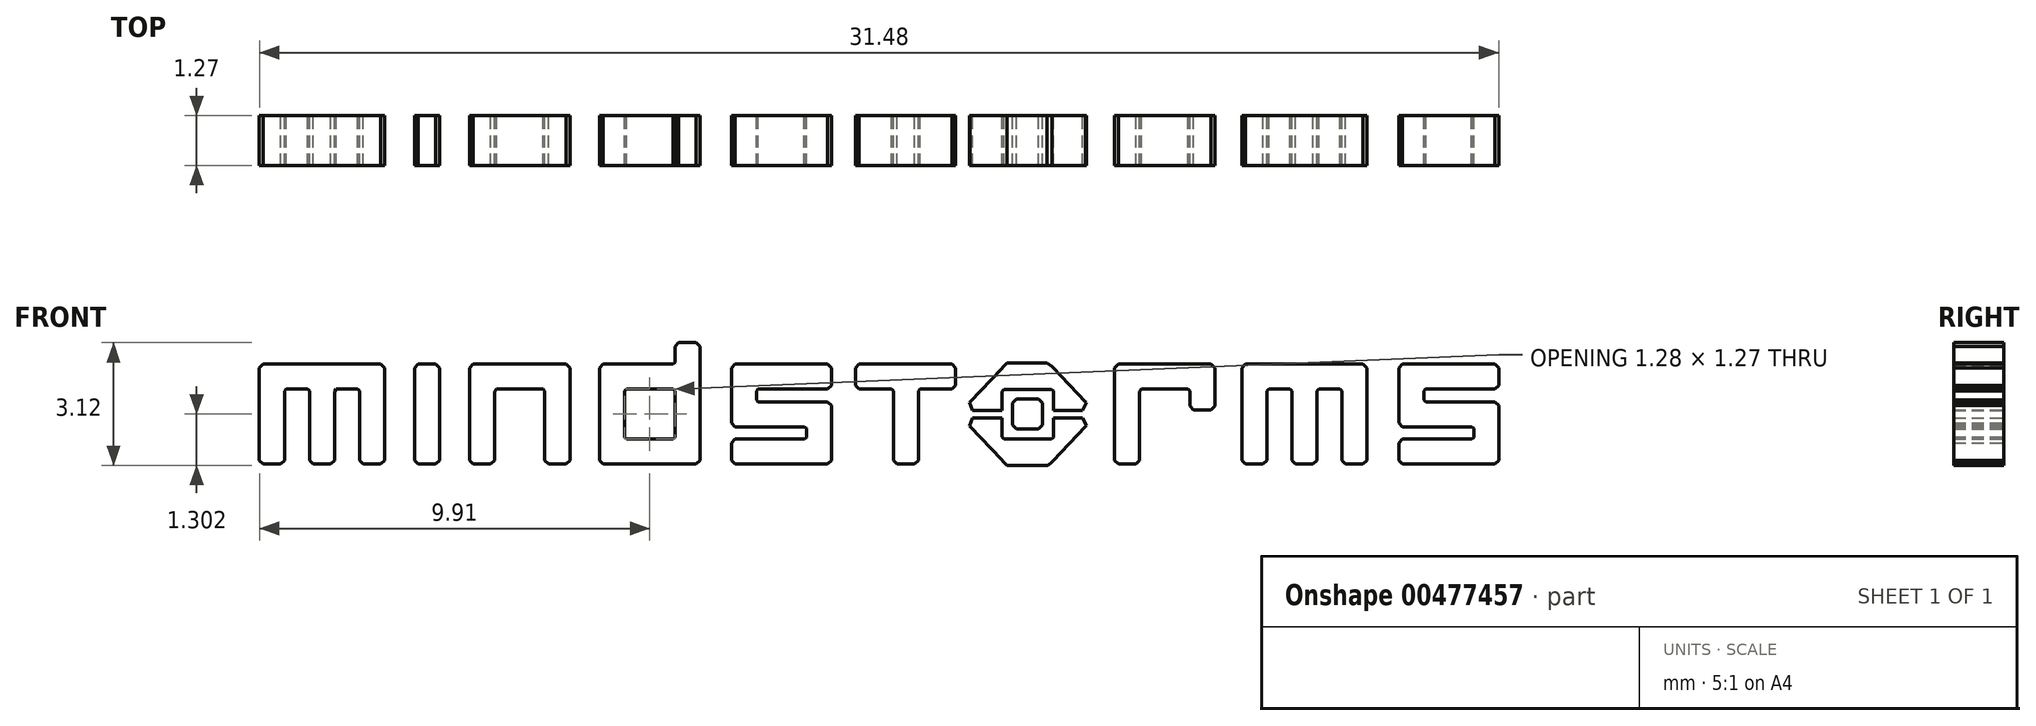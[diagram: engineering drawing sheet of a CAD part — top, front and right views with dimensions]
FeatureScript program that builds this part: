
annotation { "Feature Type Name" : "Feature", "Feature Type Description" : "" }
export const myFeature = defineFeature(function(context is Context, id is Id, definition is map)
    precondition{}
    {
        {
            var Q0;
            Q0=qCreatedBy(makeId("Front.planeOp"),FACE);
            var sketch = newSketch(context, id + "F0", { "sketchPlane" : qUnion([Q0])});
            skLineSegment(sketch, "E0", {"start": v(4.43, -0.35) * mm, "end": v(5.14, -0.35) * mm});
            skLineSegment(sketch, "E1", {"start": v(5.14, -0.35) * mm, "end": v(5.17, -0.35) * mm});
            skLineSegment(sketch, "E2", {"start": v(5.17, -0.35) * mm, "end": v(5.26, -0.55) * mm});
            skLineSegment(sketch, "E3", {"start": v(5.26, -0.55) * mm, "end": v(5.25, -0.57) * mm});
            skLineSegment(sketch, "E4", {"start": v(5.25, -0.57) * mm, "end": v(4.42, -1.44) * mm});
            skLineSegment(sketch, "E5", {"start": v(4.42, -1.44) * mm, "end": v(4.38, -1.47) * mm});
            skLineSegment(sketch, "E6", {"start": v(4.38, -1.47) * mm, "end": v(4.29, -1.56) * mm});
            skLineSegment(sketch, "E7", {"start": v(4.29, -1.56) * mm, "end": v(4.25, -1.56) * mm});
            skLineSegment(sketch, "E8", {"start": v(4.25, -1.56) * mm, "end": v(3.3, -1.56) * mm});
            skLineSegment(sketch, "E9", {"start": v(3.3, -1.56) * mm, "end": v(3.25, -1.56) * mm});
            skLineSegment(sketch, "E10", {"start": v(3.25, -1.56) * mm, "end": v(3.15, -1.46) * mm});
            skLineSegment(sketch, "E11", {"start": v(3.15, -1.46) * mm, "end": v(3.11, -1.42) * mm});
            skLineSegment(sketch, "E12", {"start": v(3.11, -1.42) * mm, "end": v(2.3, -0.57) * mm});
            skLineSegment(sketch, "E13", {"start": v(2.3, -0.57) * mm, "end": v(2.3, -0.55) * mm});
            skLineSegment(sketch, "E14", {"start": v(2.3, -0.55) * mm, "end": v(2.38, -0.35) * mm});
            skLineSegment(sketch, "E15", {"start": v(2.38, -0.35) * mm, "end": v(2.4, -0.35) * mm});
            skLineSegment(sketch, "E16", {"start": v(2.4, -0.35) * mm, "end": v(3.12, -0.35) * mm});
            skLineSegment(sketch, "E17", {"start": v(3.12, -0.35) * mm, "end": v(3.12, -0.83) * mm});
            skLineSegment(sketch, "E18", {"start": v(3.12, -0.83) * mm, "end": v(3.12, -0.84) * mm});
            skLineSegment(sketch, "E19", {"start": v(3.12, -0.84) * mm, "end": v(3.17, -0.9) * mm});
            skLineSegment(sketch, "E20", {"start": v(3.17, -0.9) * mm, "end": v(3.18, -0.9) * mm});
            skLineSegment(sketch, "E21", {"start": v(3.18, -0.9) * mm, "end": v(4.36, -0.9) * mm});
            skLineSegment(sketch, "E22", {"start": v(4.36, -0.9) * mm, "end": v(4.38, -0.9) * mm});
            skLineSegment(sketch, "E23", {"start": v(4.38, -0.9) * mm, "end": v(4.43, -0.84) * mm});
            skLineSegment(sketch, "E24", {"start": v(4.43, -0.84) * mm, "end": v(4.43, -0.83) * mm});
            skLineSegment(sketch, "E25", {"start": v(4.43, -0.83) * mm, "end": v(4.43, -0.35) * mm});
            skLineSegment(sketch, "E26", {"start": v(4.43, -0.16) * mm, "end": v(5.14, -0.16) * mm});
            skLineSegment(sketch, "E27", {"start": v(5.14, -0.16) * mm, "end": v(5.17, -0.16) * mm});
            skLineSegment(sketch, "E28", {"start": v(5.17, -0.16) * mm, "end": v(5.26, 0.04) * mm});
            skLineSegment(sketch, "E29", {"start": v(5.26, 0.04) * mm, "end": v(5.25, 0.05) * mm});
            skLineSegment(sketch, "E30", {"start": v(5.25, 0.05) * mm, "end": v(4.42, 0.93) * mm});
            skLineSegment(sketch, "E31", {"start": v(4.42, 0.93) * mm, "end": v(4.39, 0.96) * mm});
            skLineSegment(sketch, "E32", {"start": v(4.39, 0.96) * mm, "end": v(4.26, 1.05) * mm});
            skLineSegment(sketch, "E33", {"start": v(4.26, 1.05) * mm, "end": v(4.25, 1.05) * mm});
            skLineSegment(sketch, "E34", {"start": v(4.25, 1.05) * mm, "end": v(3.3, 1.05) * mm});
            skLineSegment(sketch, "E35", {"start": v(3.3, 1.05) * mm, "end": v(3.25, 1.05) * mm});
            skLineSegment(sketch, "E36", {"start": v(3.25, 1.05) * mm, "end": v(3.15, 0.94) * mm});
            skLineSegment(sketch, "E37", {"start": v(3.15, 0.94) * mm, "end": v(3.11, 0.9) * mm});
            skLineSegment(sketch, "E38", {"start": v(3.11, 0.9) * mm, "end": v(2.3, 0.05) * mm});
            skLineSegment(sketch, "E39", {"start": v(2.3, 0.05) * mm, "end": v(2.3, 0.04) * mm});
            skLineSegment(sketch, "E40", {"start": v(2.3, 0.04) * mm, "end": v(2.38, -0.16) * mm});
            skLineSegment(sketch, "E41", {"start": v(2.38, -0.16) * mm, "end": v(2.4, -0.16) * mm});
            skLineSegment(sketch, "E42", {"start": v(2.4, -0.16) * mm, "end": v(3.12, -0.16) * mm});
            skLineSegment(sketch, "E43", {"start": v(3.12, -0.16) * mm, "end": v(3.12, 0.31) * mm});
            skLineSegment(sketch, "E44", {"start": v(3.12, 0.31) * mm, "end": v(3.12, 0.32) * mm});
            skLineSegment(sketch, "E45", {"start": v(3.12, 0.32) * mm, "end": v(3.17, 0.38) * mm});
            skLineSegment(sketch, "E46", {"start": v(3.17, 0.38) * mm, "end": v(3.19, 0.38) * mm});
            skLineSegment(sketch, "E47", {"start": v(3.19, 0.38) * mm, "end": v(4.36, 0.38) * mm});
            skLineSegment(sketch, "E48", {"start": v(4.36, 0.38) * mm, "end": v(4.38, 0.38) * mm});
            skLineSegment(sketch, "E49", {"start": v(4.38, 0.38) * mm, "end": v(4.43, 0.33) * mm});
            skLineSegment(sketch, "E50", {"start": v(4.43, 0.33) * mm, "end": v(4.43, 0.31) * mm});
            skLineSegment(sketch, "E51", {"start": v(4.43, 0.31) * mm, "end": v(4.43, -0.16) * mm});
            skLineSegment(sketch, "E52", {"start": v(8.4, 1.01) * mm, "end": v(6.1, 1.01) * mm});
            skLineSegment(sketch, "E53", {"start": v(6.1, 1.01) * mm, "end": v(6.08, 1.01) * mm});
            skLineSegment(sketch, "E54", {"start": v(6.08, 1.01) * mm, "end": v(5.98, 0.92) * mm});
            skLineSegment(sketch, "E55", {"start": v(5.98, 0.92) * mm, "end": v(5.98, 0.89) * mm});
            skLineSegment(sketch, "E56", {"start": v(5.98, 0.89) * mm, "end": v(5.98, -1.4) * mm});
            skLineSegment(sketch, "E57", {"start": v(5.98, -1.4) * mm, "end": v(5.98, -1.43) * mm});
            skLineSegment(sketch, "E58", {"start": v(5.98, -1.43) * mm, "end": v(6.08, -1.53) * mm});
            skLineSegment(sketch, "E59", {"start": v(6.08, -1.53) * mm, "end": v(6.1, -1.53) * mm});
            skLineSegment(sketch, "E60", {"start": v(6.1, -1.53) * mm, "end": v(6.49, -1.53) * mm});
            skLineSegment(sketch, "E61", {"start": v(6.49, -1.53) * mm, "end": v(6.52, -1.53) * mm});
            skLineSegment(sketch, "E62", {"start": v(6.52, -1.53) * mm, "end": v(6.62, -1.43) * mm});
            skLineSegment(sketch, "E63", {"start": v(6.62, -1.43) * mm, "end": v(6.62, -1.4) * mm});
            skLineSegment(sketch, "E64", {"start": v(6.62, -1.4) * mm, "end": v(6.62, 0.32) * mm});
            skLineSegment(sketch, "E65", {"start": v(6.62, 0.32) * mm, "end": v(6.62, 0.32) * mm});
            skLineSegment(sketch, "E66", {"start": v(6.62, 0.32) * mm, "end": v(6.66, 0.38) * mm});
            skLineSegment(sketch, "E67", {"start": v(6.66, 0.38) * mm, "end": v(6.68, 0.38) * mm});
            skLineSegment(sketch, "E68", {"start": v(6.68, 0.38) * mm, "end": v(7.83, 0.38) * mm});
            skLineSegment(sketch, "E69", {"start": v(7.83, 0.38) * mm, "end": v(7.84, 0.38) * mm});
            skLineSegment(sketch, "E70", {"start": v(7.84, 0.38) * mm, "end": v(7.9, 0.33) * mm});
            skLineSegment(sketch, "E71", {"start": v(7.9, 0.33) * mm, "end": v(7.9, 0.32) * mm});
            skLineSegment(sketch, "E72", {"start": v(7.9, 0.32) * mm, "end": v(7.9, -0.02) * mm});
            skLineSegment(sketch, "E73", {"start": v(7.9, -0.02) * mm, "end": v(7.9, -0.05) * mm});
            skLineSegment(sketch, "E74", {"start": v(7.9, -0.05) * mm, "end": v(7.99, -0.15) * mm});
            skLineSegment(sketch, "E75", {"start": v(7.99, -0.15) * mm, "end": v(8.02, -0.15) * mm});
            skLineSegment(sketch, "E76", {"start": v(8.02, -0.15) * mm, "end": v(8.4, -0.15) * mm});
            skLineSegment(sketch, "E77", {"start": v(8.4, -0.15) * mm, "end": v(8.43, -0.15) * mm});
            skLineSegment(sketch, "E78", {"start": v(8.43, -0.15) * mm, "end": v(8.53, -0.05) * mm});
            skLineSegment(sketch, "E79", {"start": v(8.53, -0.05) * mm, "end": v(8.53, -0.02) * mm});
            skLineSegment(sketch, "E80", {"start": v(8.53, -0.02) * mm, "end": v(8.53, 0.89) * mm});
            skLineSegment(sketch, "E81", {"start": v(8.53, 0.89) * mm, "end": v(8.53, 0.92) * mm});
            skLineSegment(sketch, "E82", {"start": v(8.53, 0.92) * mm, "end": v(8.43, 1.01) * mm});
            skLineSegment(sketch, "E83", {"start": v(8.43, 1.01) * mm, "end": v(8.4, 1.01) * mm});
            skLineSegment(sketch, "E84", {"start": v(13.84, 0.32) * mm, "end": v(13.84, 0.33) * mm});
            skLineSegment(sketch, "E85", {"start": v(13.84, 0.33) * mm, "end": v(13.88, 0.38) * mm});
            skLineSegment(sketch, "E86", {"start": v(13.88, 0.38) * mm, "end": v(13.9, 0.38) * mm});
            skLineSegment(sketch, "E87", {"start": v(13.9, 0.38) * mm, "end": v(15.62, 0.38) * mm});
            skLineSegment(sketch, "E88", {"start": v(15.62, 0.38) * mm, "end": v(15.65, 0.38) * mm});
            skLineSegment(sketch, "E89", {"start": v(15.65, 0.38) * mm, "end": v(15.74, 0.47) * mm});
            skLineSegment(sketch, "E90", {"start": v(15.74, 0.47) * mm, "end": v(15.74, 0.5) * mm});
            skLineSegment(sketch, "E91", {"start": v(15.74, 0.5) * mm, "end": v(15.74, 0.89) * mm});
            skLineSegment(sketch, "E92", {"start": v(15.74, 0.89) * mm, "end": v(15.74, 0.92) * mm});
            skLineSegment(sketch, "E93", {"start": v(15.74, 0.92) * mm, "end": v(15.65, 1.01) * mm});
            skLineSegment(sketch, "E94", {"start": v(15.65, 1.01) * mm, "end": v(15.62, 1.01) * mm});
            skLineSegment(sketch, "E95", {"start": v(15.62, 1.01) * mm, "end": v(13.33, 1.01) * mm});
            skLineSegment(sketch, "E96", {"start": v(13.33, 1.01) * mm, "end": v(13.3, 1.01) * mm});
            skLineSegment(sketch, "E97", {"start": v(13.3, 1.01) * mm, "end": v(13.2, 0.92) * mm});
            skLineSegment(sketch, "E98", {"start": v(13.2, 0.92) * mm, "end": v(13.2, 0.89) * mm});
            skLineSegment(sketch, "E99", {"start": v(13.2, 0.89) * mm, "end": v(13.2, -0.45) * mm});
            skLineSegment(sketch, "E100", {"start": v(13.2, -0.45) * mm, "end": v(13.2, -0.48) * mm});
            skLineSegment(sketch, "E101", {"start": v(13.2, -0.48) * mm, "end": v(13.3, -0.58) * mm});
            skLineSegment(sketch, "E102", {"start": v(13.3, -0.58) * mm, "end": v(13.33, -0.58) * mm});
            skLineSegment(sketch, "E103", {"start": v(13.33, -0.58) * mm, "end": v(15.05, -0.58) * mm});
            skLineSegment(sketch, "E104", {"start": v(15.05, -0.58) * mm, "end": v(15.06, -0.58) * mm});
            skLineSegment(sketch, "E105", {"start": v(15.06, -0.58) * mm, "end": v(15.1, -0.62) * mm});
            skLineSegment(sketch, "E106", {"start": v(15.1, -0.62) * mm, "end": v(15.1, -0.64) * mm});
            skLineSegment(sketch, "E107", {"start": v(15.1, -0.64) * mm, "end": v(15.1, -0.83) * mm});
            skLineSegment(sketch, "E108", {"start": v(15.1, -0.83) * mm, "end": v(15.1, -0.85) * mm});
            skLineSegment(sketch, "E109", {"start": v(15.1, -0.85) * mm, "end": v(15.06, -0.9) * mm});
            skLineSegment(sketch, "E110", {"start": v(15.06, -0.9) * mm, "end": v(15.05, -0.9) * mm});
            skLineSegment(sketch, "E111", {"start": v(15.05, -0.9) * mm, "end": v(13.33, -0.9) * mm});
            skLineSegment(sketch, "E112", {"start": v(13.33, -0.9) * mm, "end": v(13.3, -0.9) * mm});
            skLineSegment(sketch, "E113", {"start": v(13.3, -0.9) * mm, "end": v(13.2, -1) * mm});
            skLineSegment(sketch, "E114", {"start": v(13.2, -1) * mm, "end": v(13.2, -1.02) * mm});
            skLineSegment(sketch, "E115", {"start": v(13.2, -1.02) * mm, "end": v(13.2, -1.4) * mm});
            skLineSegment(sketch, "E116", {"start": v(13.2, -1.4) * mm, "end": v(13.2, -1.43) * mm});
            skLineSegment(sketch, "E117", {"start": v(13.2, -1.43) * mm, "end": v(13.3, -1.53) * mm});
            skLineSegment(sketch, "E118", {"start": v(13.3, -1.53) * mm, "end": v(13.33, -1.53) * mm});
            skLineSegment(sketch, "E119", {"start": v(13.33, -1.53) * mm, "end": v(15.62, -1.53) * mm});
            skLineSegment(sketch, "E120", {"start": v(15.62, -1.53) * mm, "end": v(15.65, -1.53) * mm});
            skLineSegment(sketch, "E121", {"start": v(15.65, -1.53) * mm, "end": v(15.74, -1.43) * mm});
            skLineSegment(sketch, "E122", {"start": v(15.74, -1.43) * mm, "end": v(15.74, -1.4) * mm});
            skLineSegment(sketch, "E123", {"start": v(15.74, -1.4) * mm, "end": v(15.74, -0.07) * mm});
            skLineSegment(sketch, "E124", {"start": v(15.74, -0.07) * mm, "end": v(15.74, -0.04) * mm});
            skLineSegment(sketch, "E125", {"start": v(15.74, -0.04) * mm, "end": v(15.65, 0.06) * mm});
            skLineSegment(sketch, "E126", {"start": v(15.65, 0.06) * mm, "end": v(15.62, 0.06) * mm});
            skLineSegment(sketch, "E127", {"start": v(15.62, 0.06) * mm, "end": v(13.9, 0.06) * mm});
            skLineSegment(sketch, "E128", {"start": v(13.9, 0.06) * mm, "end": v(13.88, 0.06) * mm});
            skLineSegment(sketch, "E129", {"start": v(13.88, 0.06) * mm, "end": v(13.84, 0.1) * mm});
            skLineSegment(sketch, "E130", {"start": v(13.84, 0.1) * mm, "end": v(13.84, 0.12) * mm});
            skLineSegment(sketch, "E131", {"start": v(13.84, 0.12) * mm, "end": v(13.84, 0.32) * mm});
            skLineSegment(sketch, "E132", {"start": v(-3.12, 0.32) * mm, "end": v(-3.12, 0.33) * mm});
            skLineSegment(sketch, "E133", {"start": v(-3.12, 0.33) * mm, "end": v(-3.08, 0.38) * mm});
            skLineSegment(sketch, "E134", {"start": v(-3.08, 0.38) * mm, "end": v(-3.06, 0.38) * mm});
            skLineSegment(sketch, "E135", {"start": v(-3.06, 0.38) * mm, "end": v(-1.34, 0.38) * mm});
            skLineSegment(sketch, "E136", {"start": v(-1.34, 0.38) * mm, "end": v(-1.31, 0.38) * mm});
            skLineSegment(sketch, "E137", {"start": v(-1.31, 0.38) * mm, "end": v(-1.21, 0.47) * mm});
            skLineSegment(sketch, "E138", {"start": v(-1.21, 0.47) * mm, "end": v(-1.21, 0.5) * mm});
            skLineSegment(sketch, "E139", {"start": v(-1.21, 0.5) * mm, "end": v(-1.21, 0.89) * mm});
            skLineSegment(sketch, "E140", {"start": v(-1.21, 0.89) * mm, "end": v(-1.21, 0.92) * mm});
            skLineSegment(sketch, "E141", {"start": v(-1.21, 0.92) * mm, "end": v(-1.31, 1.01) * mm});
            skLineSegment(sketch, "E142", {"start": v(-1.31, 1.01) * mm, "end": v(-1.34, 1.01) * mm});
            skLineSegment(sketch, "E143", {"start": v(-1.34, 1.01) * mm, "end": v(-3.63, 1.01) * mm});
            skLineSegment(sketch, "E144", {"start": v(-3.63, 1.01) * mm, "end": v(-3.66, 1.01) * mm});
            skLineSegment(sketch, "E145", {"start": v(-3.66, 1.01) * mm, "end": v(-3.76, 0.92) * mm});
            skLineSegment(sketch, "E146", {"start": v(-3.76, 0.92) * mm, "end": v(-3.76, 0.89) * mm});
            skLineSegment(sketch, "E147", {"start": v(-3.76, 0.89) * mm, "end": v(-3.76, -0.45) * mm});
            skLineSegment(sketch, "E148", {"start": v(-3.76, -0.45) * mm, "end": v(-3.76, -0.48) * mm});
            skLineSegment(sketch, "E149", {"start": v(-3.76, -0.48) * mm, "end": v(-3.66, -0.58) * mm});
            skLineSegment(sketch, "E150", {"start": v(-3.66, -0.58) * mm, "end": v(-3.63, -0.58) * mm});
            skLineSegment(sketch, "E151", {"start": v(-3.63, -0.58) * mm, "end": v(-1.9, -0.58) * mm});
            skLineSegment(sketch, "E152", {"start": v(-1.9, -0.58) * mm, "end": v(-1.9, -0.58) * mm});
            skLineSegment(sketch, "E153", {"start": v(-1.9, -0.58) * mm, "end": v(-1.85, -0.62) * mm});
            skLineSegment(sketch, "E154", {"start": v(-1.85, -0.62) * mm, "end": v(-1.85, -0.64) * mm});
            skLineSegment(sketch, "E155", {"start": v(-1.85, -0.64) * mm, "end": v(-1.85, -0.83) * mm});
            skLineSegment(sketch, "E156", {"start": v(-1.85, -0.83) * mm, "end": v(-1.85, -0.85) * mm});
            skLineSegment(sketch, "E157", {"start": v(-1.85, -0.85) * mm, "end": v(-1.9, -0.9) * mm});
            skLineSegment(sketch, "E158", {"start": v(-1.9, -0.9) * mm, "end": v(-1.9, -0.9) * mm});
            skLineSegment(sketch, "E159", {"start": v(-1.9, -0.9) * mm, "end": v(-3.63, -0.9) * mm});
            skLineSegment(sketch, "E160", {"start": v(-3.63, -0.9) * mm, "end": v(-3.66, -0.9) * mm});
            skLineSegment(sketch, "E161", {"start": v(-3.66, -0.9) * mm, "end": v(-3.76, -1) * mm});
            skLineSegment(sketch, "E162", {"start": v(-3.76, -1) * mm, "end": v(-3.76, -1.02) * mm});
            skLineSegment(sketch, "E163", {"start": v(-3.76, -1.02) * mm, "end": v(-3.76, -1.4) * mm});
            skLineSegment(sketch, "E164", {"start": v(-3.76, -1.4) * mm, "end": v(-3.76, -1.43) * mm});
            skLineSegment(sketch, "E165", {"start": v(-3.76, -1.43) * mm, "end": v(-3.66, -1.53) * mm});
            skLineSegment(sketch, "E166", {"start": v(-3.66, -1.53) * mm, "end": v(-3.63, -1.53) * mm});
            skLineSegment(sketch, "E167", {"start": v(-3.63, -1.53) * mm, "end": v(-1.34, -1.53) * mm});
            skLineSegment(sketch, "E168", {"start": v(-1.34, -1.53) * mm, "end": v(-1.31, -1.53) * mm});
            skLineSegment(sketch, "E169", {"start": v(-1.31, -1.53) * mm, "end": v(-1.21, -1.43) * mm});
            skLineSegment(sketch, "E170", {"start": v(-1.21, -1.43) * mm, "end": v(-1.21, -1.4) * mm});
            skLineSegment(sketch, "E171", {"start": v(-1.21, -1.4) * mm, "end": v(-1.21, -0.07) * mm});
            skLineSegment(sketch, "E172", {"start": v(-1.21, -0.07) * mm, "end": v(-1.21, -0.04) * mm});
            skLineSegment(sketch, "E173", {"start": v(-1.21, -0.04) * mm, "end": v(-1.31, 0.06) * mm});
            skLineSegment(sketch, "E174", {"start": v(-1.31, 0.06) * mm, "end": v(-1.34, 0.06) * mm});
            skLineSegment(sketch, "E175", {"start": v(-1.34, 0.06) * mm, "end": v(-3.06, 0.06) * mm});
            skLineSegment(sketch, "E176", {"start": v(-3.06, 0.06) * mm, "end": v(-3.07, 0.06) * mm});
            skLineSegment(sketch, "E177", {"start": v(-3.07, 0.06) * mm, "end": v(-3.12, 0.1) * mm});
            skLineSegment(sketch, "E178", {"start": v(-3.12, 0.1) * mm, "end": v(-3.12, 0.12) * mm});
            skLineSegment(sketch, "E179", {"start": v(-3.12, 0.12) * mm, "end": v(-3.12, 0.32) * mm});
            skLineSegment(sketch, "E180", {"start": v(-5.2, -0.83) * mm, "end": v(-5.2, -0.85) * mm});
            skLineSegment(sketch, "E181", {"start": v(-5.2, -0.85) * mm, "end": v(-5.24, -0.9) * mm});
            skLineSegment(sketch, "E182", {"start": v(-5.24, -0.9) * mm, "end": v(-5.25, -0.9) * mm});
            skLineSegment(sketch, "E183", {"start": v(-5.25, -0.9) * mm, "end": v(-6.4, -0.9) * mm});
            skLineSegment(sketch, "E184", {"start": v(-6.4, -0.9) * mm, "end": v(-6.42, -0.9) * mm});
            skLineSegment(sketch, "E185", {"start": v(-6.42, -0.9) * mm, "end": v(-6.47, -0.85) * mm});
            skLineSegment(sketch, "E186", {"start": v(-6.47, -0.85) * mm, "end": v(-6.47, -0.83) * mm});
            skLineSegment(sketch, "E187", {"start": v(-6.47, -0.83) * mm, "end": v(-6.47, 0.32) * mm});
            skLineSegment(sketch, "E188", {"start": v(-6.47, 0.32) * mm, "end": v(-6.47, 0.33) * mm});
            skLineSegment(sketch, "E189", {"start": v(-6.47, 0.33) * mm, "end": v(-6.42, 0.38) * mm});
            skLineSegment(sketch, "E190", {"start": v(-6.42, 0.38) * mm, "end": v(-6.4, 0.38) * mm});
            skLineSegment(sketch, "E191", {"start": v(-6.4, 0.38) * mm, "end": v(-5.25, 0.38) * mm});
            skLineSegment(sketch, "E192", {"start": v(-5.25, 0.38) * mm, "end": v(-5.24, 0.38) * mm});
            skLineSegment(sketch, "E193", {"start": v(-5.24, 0.38) * mm, "end": v(-5.2, 0.33) * mm});
            skLineSegment(sketch, "E194", {"start": v(-5.2, 0.33) * mm, "end": v(-5.2, 0.32) * mm});
            skLineSegment(sketch, "E195", {"start": v(-5.2, 0.32) * mm, "end": v(-5.2, -0.83) * mm});
            skLineSegment(sketch, "E196", {"start": v(-4.68, 1.56) * mm, "end": v(-5.06, 1.56) * mm});
            skLineSegment(sketch, "E197", {"start": v(-5.06, 1.56) * mm, "end": v(-5.1, 1.56) * mm});
            skLineSegment(sketch, "E198", {"start": v(-5.1, 1.56) * mm, "end": v(-5.2, 1.47) * mm});
            skLineSegment(sketch, "E199", {"start": v(-5.2, 1.47) * mm, "end": v(-5.2, 1.43) * mm});
            skLineSegment(sketch, "E200", {"start": v(-5.2, 1.43) * mm, "end": v(-5.2, 1.08) * mm});
            skLineSegment(sketch, "E201", {"start": v(-5.2, 1.08) * mm, "end": v(-5.2, 1.06) * mm});
            skLineSegment(sketch, "E202", {"start": v(-5.2, 1.06) * mm, "end": v(-5.24, 1.01) * mm});
            skLineSegment(sketch, "E203", {"start": v(-5.24, 1.01) * mm, "end": v(-5.25, 1.01) * mm});
            skLineSegment(sketch, "E204", {"start": v(-5.25, 1.01) * mm, "end": v(-6.98, 1.01) * mm});
            skLineSegment(sketch, "E205", {"start": v(-6.98, 1.01) * mm, "end": v(-7.01, 1.01) * mm});
            skLineSegment(sketch, "E206", {"start": v(-7.01, 1.01) * mm, "end": v(-7.1, 0.92) * mm});
            skLineSegment(sketch, "E207", {"start": v(-7.1, 0.92) * mm, "end": v(-7.1, 0.89) * mm});
            skLineSegment(sketch, "E208", {"start": v(-7.1, 0.89) * mm, "end": v(-7.1, -1.4) * mm});
            skLineSegment(sketch, "E209", {"start": v(-7.1, -1.4) * mm, "end": v(-7.1, -1.43) * mm});
            skLineSegment(sketch, "E210", {"start": v(-7.1, -1.43) * mm, "end": v(-7.01, -1.53) * mm});
            skLineSegment(sketch, "E211", {"start": v(-7.01, -1.53) * mm, "end": v(-6.98, -1.53) * mm});
            skLineSegment(sketch, "E212", {"start": v(-6.98, -1.53) * mm, "end": v(-4.68, -1.53) * mm});
            skLineSegment(sketch, "E213", {"start": v(-4.68, -1.53) * mm, "end": v(-4.65, -1.53) * mm});
            skLineSegment(sketch, "E214", {"start": v(-4.65, -1.53) * mm, "end": v(-4.56, -1.43) * mm});
            skLineSegment(sketch, "E215", {"start": v(-4.56, -1.43) * mm, "end": v(-4.56, -1.4) * mm});
            skLineSegment(sketch, "E216", {"start": v(-4.56, -1.4) * mm, "end": v(-4.56, 1.43) * mm});
            skLineSegment(sketch, "E217", {"start": v(-4.56, 1.43) * mm, "end": v(-4.56, 1.47) * mm});
            skLineSegment(sketch, "E218", {"start": v(-4.56, 1.47) * mm, "end": v(-4.65, 1.56) * mm});
            skLineSegment(sketch, "E219", {"start": v(-4.65, 1.56) * mm, "end": v(-4.68, 1.56) * mm});
            skLineSegment(sketch, "E220", {"start": v(1.81, 1.01) * mm, "end": v(-0.47, 1.01) * mm});
            skLineSegment(sketch, "E221", {"start": v(-0.47, 1.01) * mm, "end": v(-0.5, 1.01) * mm});
            skLineSegment(sketch, "E222", {"start": v(-0.5, 1.01) * mm, "end": v(-0.6, 0.92) * mm});
            skLineSegment(sketch, "E223", {"start": v(-0.6, 0.92) * mm, "end": v(-0.6, 0.89) * mm});
            skLineSegment(sketch, "E224", {"start": v(-0.6, 0.89) * mm, "end": v(-0.6, 0.5) * mm});
            skLineSegment(sketch, "E225", {"start": v(-0.6, 0.5) * mm, "end": v(-0.6, 0.47) * mm});
            skLineSegment(sketch, "E226", {"start": v(-0.6, 0.47) * mm, "end": v(-0.5, 0.38) * mm});
            skLineSegment(sketch, "E227", {"start": v(-0.5, 0.38) * mm, "end": v(-0.47, 0.38) * mm});
            skLineSegment(sketch, "E228", {"start": v(-0.47, 0.38) * mm, "end": v(0.3, 0.38) * mm});
            skLineSegment(sketch, "E229", {"start": v(0.3, 0.38) * mm, "end": v(0.31, 0.38) * mm});
            skLineSegment(sketch, "E230", {"start": v(0.31, 0.38) * mm, "end": v(0.36, 0.33) * mm});
            skLineSegment(sketch, "E231", {"start": v(0.36, 0.33) * mm, "end": v(0.36, 0.32) * mm});
            skLineSegment(sketch, "E232", {"start": v(0.36, 0.32) * mm, "end": v(0.36, -1.4) * mm});
            skLineSegment(sketch, "E233", {"start": v(0.36, -1.4) * mm, "end": v(0.36, -1.43) * mm});
            skLineSegment(sketch, "E234", {"start": v(0.36, -1.43) * mm, "end": v(0.45, -1.53) * mm});
            skLineSegment(sketch, "E235", {"start": v(0.45, -1.53) * mm, "end": v(0.49, -1.53) * mm});
            skLineSegment(sketch, "E236", {"start": v(0.49, -1.53) * mm, "end": v(0.87, -1.53) * mm});
            skLineSegment(sketch, "E237", {"start": v(0.87, -1.53) * mm, "end": v(0.9, -1.53) * mm});
            skLineSegment(sketch, "E238", {"start": v(0.9, -1.53) * mm, "end": v(1, -1.43) * mm});
            skLineSegment(sketch, "E239", {"start": v(1, -1.43) * mm, "end": v(1, -1.4) * mm});
            skLineSegment(sketch, "E240", {"start": v(1, -1.4) * mm, "end": v(1, 0.32) * mm});
            skLineSegment(sketch, "E241", {"start": v(1, 0.32) * mm, "end": v(1, 0.33) * mm});
            skLineSegment(sketch, "E242", {"start": v(1, 0.33) * mm, "end": v(1.04, 0.38) * mm});
            skLineSegment(sketch, "E243", {"start": v(1.04, 0.38) * mm, "end": v(1.06, 0.38) * mm});
            skLineSegment(sketch, "E244", {"start": v(1.06, 0.38) * mm, "end": v(1.81, 0.38) * mm});
            skLineSegment(sketch, "E245", {"start": v(1.81, 0.38) * mm, "end": v(1.84, 0.38) * mm});
            skLineSegment(sketch, "E246", {"start": v(1.84, 0.38) * mm, "end": v(1.94, 0.47) * mm});
            skLineSegment(sketch, "E247", {"start": v(1.94, 0.47) * mm, "end": v(1.94, 0.5) * mm});
            skLineSegment(sketch, "E248", {"start": v(1.94, 0.5) * mm, "end": v(1.94, 0.89) * mm});
            skLineSegment(sketch, "E249", {"start": v(1.94, 0.89) * mm, "end": v(1.94, 0.92) * mm});
            skLineSegment(sketch, "E250", {"start": v(1.94, 0.92) * mm, "end": v(1.84, 1.01) * mm});
            skLineSegment(sketch, "E251", {"start": v(1.84, 1.01) * mm, "end": v(1.81, 1.01) * mm});
            skLineSegment(sketch, "E252", {"start": v(-7.98, 1.01) * mm, "end": v(-10.28, 1.01) * mm});
            skLineSegment(sketch, "E253", {"start": v(-10.28, 1.01) * mm, "end": v(-10.31, 1.01) * mm});
            skLineSegment(sketch, "E254", {"start": v(-10.31, 1.01) * mm, "end": v(-10.4, 0.92) * mm});
            skLineSegment(sketch, "E255", {"start": v(-10.4, 0.92) * mm, "end": v(-10.4, 0.89) * mm});
            skLineSegment(sketch, "E256", {"start": v(-10.4, 0.89) * mm, "end": v(-10.4, -1.4) * mm});
            skLineSegment(sketch, "E257", {"start": v(-10.4, -1.4) * mm, "end": v(-10.4, -1.43) * mm});
            skLineSegment(sketch, "E258", {"start": v(-10.4, -1.43) * mm, "end": v(-10.31, -1.53) * mm});
            skLineSegment(sketch, "E259", {"start": v(-10.31, -1.53) * mm, "end": v(-10.28, -1.53) * mm});
            skLineSegment(sketch, "E260", {"start": v(-10.28, -1.53) * mm, "end": v(-9.9, -1.53) * mm});
            skLineSegment(sketch, "E261", {"start": v(-9.9, -1.53) * mm, "end": v(-9.87, -1.53) * mm});
            skLineSegment(sketch, "E262", {"start": v(-9.87, -1.53) * mm, "end": v(-9.77, -1.43) * mm});
            skLineSegment(sketch, "E263", {"start": v(-9.77, -1.43) * mm, "end": v(-9.77, -1.4) * mm});
            skLineSegment(sketch, "E264", {"start": v(-9.77, -1.4) * mm, "end": v(-9.77, 0.32) * mm});
            skLineSegment(sketch, "E265", {"start": v(-9.77, 0.32) * mm, "end": v(-9.77, 0.32) * mm});
            skLineSegment(sketch, "E266", {"start": v(-9.77, 0.32) * mm, "end": v(-9.72, 0.38) * mm});
            skLineSegment(sketch, "E267", {"start": v(-9.72, 0.38) * mm, "end": v(-9.7, 0.38) * mm});
            skLineSegment(sketch, "E268", {"start": v(-9.7, 0.38) * mm, "end": v(-8.56, 0.38) * mm});
            skLineSegment(sketch, "E269", {"start": v(-8.56, 0.38) * mm, "end": v(-8.54, 0.38) * mm});
            skLineSegment(sketch, "E270", {"start": v(-8.54, 0.38) * mm, "end": v(-8.5, 0.33) * mm});
            skLineSegment(sketch, "E271", {"start": v(-8.5, 0.33) * mm, "end": v(-8.5, 0.32) * mm});
            skLineSegment(sketch, "E272", {"start": v(-8.5, 0.32) * mm, "end": v(-8.5, -1.4) * mm});
            skLineSegment(sketch, "E273", {"start": v(-8.5, -1.4) * mm, "end": v(-8.5, -1.43) * mm});
            skLineSegment(sketch, "E274", {"start": v(-8.5, -1.43) * mm, "end": v(-8.4, -1.53) * mm});
            skLineSegment(sketch, "E275", {"start": v(-8.4, -1.53) * mm, "end": v(-8.37, -1.53) * mm});
            skLineSegment(sketch, "E276", {"start": v(-8.37, -1.53) * mm, "end": v(-7.98, -1.53) * mm});
            skLineSegment(sketch, "E277", {"start": v(-7.98, -1.53) * mm, "end": v(-7.95, -1.53) * mm});
            skLineSegment(sketch, "E278", {"start": v(-7.95, -1.53) * mm, "end": v(-7.86, -1.43) * mm});
            skLineSegment(sketch, "E279", {"start": v(-7.86, -1.43) * mm, "end": v(-7.86, -1.4) * mm});
            skLineSegment(sketch, "E280", {"start": v(-7.86, -1.4) * mm, "end": v(-7.86, 0.89) * mm});
            skLineSegment(sketch, "E281", {"start": v(-7.86, 0.89) * mm, "end": v(-7.86, 0.92) * mm});
            skLineSegment(sketch, "E282", {"start": v(-7.86, 0.92) * mm, "end": v(-7.95, 1.01) * mm});
            skLineSegment(sketch, "E283", {"start": v(-7.95, 1.01) * mm, "end": v(-7.98, 1.01) * mm});
            skLineSegment(sketch, "E284", {"start": v(12.26, 1.01) * mm, "end": v(9.34, 1.01) * mm});
            skLineSegment(sketch, "E285", {"start": v(9.34, 1.01) * mm, "end": v(9.31, 1.01) * mm});
            skLineSegment(sketch, "E286", {"start": v(9.31, 1.01) * mm, "end": v(9.21, 0.92) * mm});
            skLineSegment(sketch, "E287", {"start": v(9.21, 0.92) * mm, "end": v(9.21, 0.89) * mm});
            skLineSegment(sketch, "E288", {"start": v(9.21, 0.89) * mm, "end": v(9.21, -1.4) * mm});
            skLineSegment(sketch, "E289", {"start": v(9.21, -1.4) * mm, "end": v(9.21, -1.43) * mm});
            skLineSegment(sketch, "E290", {"start": v(9.21, -1.43) * mm, "end": v(9.31, -1.53) * mm});
            skLineSegment(sketch, "E291", {"start": v(9.31, -1.53) * mm, "end": v(9.34, -1.53) * mm});
            skLineSegment(sketch, "E292", {"start": v(9.34, -1.53) * mm, "end": v(9.72, -1.53) * mm});
            skLineSegment(sketch, "E293", {"start": v(9.72, -1.53) * mm, "end": v(9.75, -1.53) * mm});
            skLineSegment(sketch, "E294", {"start": v(9.75, -1.53) * mm, "end": v(9.85, -1.43) * mm});
            skLineSegment(sketch, "E295", {"start": v(9.85, -1.43) * mm, "end": v(9.85, -1.4) * mm});
            skLineSegment(sketch, "E296", {"start": v(9.85, -1.4) * mm, "end": v(9.85, 0.32) * mm});
            skLineSegment(sketch, "E297", {"start": v(9.85, 0.32) * mm, "end": v(9.85, 0.33) * mm});
            skLineSegment(sketch, "E298", {"start": v(9.85, 0.33) * mm, "end": v(9.9, 0.38) * mm});
            skLineSegment(sketch, "E299", {"start": v(9.9, 0.38) * mm, "end": v(9.91, 0.38) * mm});
            skLineSegment(sketch, "E300", {"start": v(9.91, 0.38) * mm, "end": v(10.42, 0.38) * mm});
            skLineSegment(sketch, "E301", {"start": v(10.42, 0.38) * mm, "end": v(10.44, 0.38) * mm});
            skLineSegment(sketch, "E302", {"start": v(10.44, 0.38) * mm, "end": v(10.48, 0.33) * mm});
            skLineSegment(sketch, "E303", {"start": v(10.48, 0.33) * mm, "end": v(10.48, 0.32) * mm});
            skLineSegment(sketch, "E304", {"start": v(10.48, 0.32) * mm, "end": v(10.48, -1.4) * mm});
            skLineSegment(sketch, "E305", {"start": v(10.48, -1.4) * mm, "end": v(10.48, -1.43) * mm});
            skLineSegment(sketch, "E306", {"start": v(10.48, -1.43) * mm, "end": v(10.58, -1.53) * mm});
            skLineSegment(sketch, "E307", {"start": v(10.58, -1.53) * mm, "end": v(10.61, -1.53) * mm});
            skLineSegment(sketch, "E308", {"start": v(10.61, -1.53) * mm, "end": v(11, -1.53) * mm});
            skLineSegment(sketch, "E309", {"start": v(11, -1.53) * mm, "end": v(11.02, -1.53) * mm});
            skLineSegment(sketch, "E310", {"start": v(11.02, -1.53) * mm, "end": v(11.12, -1.43) * mm});
            skLineSegment(sketch, "E311", {"start": v(11.12, -1.43) * mm, "end": v(11.12, -1.4) * mm});
            skLineSegment(sketch, "E312", {"start": v(11.12, -1.4) * mm, "end": v(11.12, 0.32) * mm});
            skLineSegment(sketch, "E313", {"start": v(11.12, 0.32) * mm, "end": v(11.12, 0.33) * mm});
            skLineSegment(sketch, "E314", {"start": v(11.12, 0.33) * mm, "end": v(11.17, 0.38) * mm});
            skLineSegment(sketch, "E315", {"start": v(11.17, 0.38) * mm, "end": v(11.18, 0.38) * mm});
            skLineSegment(sketch, "E316", {"start": v(11.18, 0.38) * mm, "end": v(11.7, 0.38) * mm});
            skLineSegment(sketch, "E317", {"start": v(11.7, 0.38) * mm, "end": v(11.7, 0.38) * mm});
            skLineSegment(sketch, "E318", {"start": v(11.7, 0.38) * mm, "end": v(11.76, 0.33) * mm});
            skLineSegment(sketch, "E319", {"start": v(11.76, 0.33) * mm, "end": v(11.76, 0.32) * mm});
            skLineSegment(sketch, "E320", {"start": v(11.76, 0.32) * mm, "end": v(11.76, -1.4) * mm});
            skLineSegment(sketch, "E321", {"start": v(11.76, -1.4) * mm, "end": v(11.76, -1.43) * mm});
            skLineSegment(sketch, "E322", {"start": v(11.76, -1.43) * mm, "end": v(11.85, -1.53) * mm});
            skLineSegment(sketch, "E323", {"start": v(11.85, -1.53) * mm, "end": v(11.88, -1.53) * mm});
            skLineSegment(sketch, "E324", {"start": v(11.88, -1.53) * mm, "end": v(12.26, -1.53) * mm});
            skLineSegment(sketch, "E325", {"start": v(12.26, -1.53) * mm, "end": v(12.3, -1.53) * mm});
            skLineSegment(sketch, "E326", {"start": v(12.3, -1.53) * mm, "end": v(12.4, -1.43) * mm});
            skLineSegment(sketch, "E327", {"start": v(12.4, -1.43) * mm, "end": v(12.4, -1.4) * mm});
            skLineSegment(sketch, "E328", {"start": v(12.4, -1.4) * mm, "end": v(12.4, 0.89) * mm});
            skLineSegment(sketch, "E329", {"start": v(12.4, 0.89) * mm, "end": v(12.4, 0.92) * mm});
            skLineSegment(sketch, "E330", {"start": v(12.4, 0.92) * mm, "end": v(12.3, 1.01) * mm});
            skLineSegment(sketch, "E331", {"start": v(12.3, 1.01) * mm, "end": v(12.26, 1.01) * mm});
            skLineSegment(sketch, "E332", {"start": v(-12.7, 1.01) * mm, "end": v(-15.62, 1.01) * mm});
            skLineSegment(sketch, "E333", {"start": v(-15.62, 1.01) * mm, "end": v(-15.65, 1.01) * mm});
            skLineSegment(sketch, "E334", {"start": v(-15.65, 1.01) * mm, "end": v(-15.74, 0.92) * mm});
            skLineSegment(sketch, "E335", {"start": v(-15.74, 0.92) * mm, "end": v(-15.74, 0.89) * mm});
            skLineSegment(sketch, "E336", {"start": v(-15.74, 0.89) * mm, "end": v(-15.74, -1.4) * mm});
            skLineSegment(sketch, "E337", {"start": v(-15.74, -1.4) * mm, "end": v(-15.74, -1.43) * mm});
            skLineSegment(sketch, "E338", {"start": v(-15.74, -1.43) * mm, "end": v(-15.65, -1.53) * mm});
            skLineSegment(sketch, "E339", {"start": v(-15.65, -1.53) * mm, "end": v(-15.62, -1.53) * mm});
            skLineSegment(sketch, "E340", {"start": v(-15.62, -1.53) * mm, "end": v(-15.24, -1.53) * mm});
            skLineSegment(sketch, "E341", {"start": v(-15.24, -1.53) * mm, "end": v(-15.2, -1.53) * mm});
            skLineSegment(sketch, "E342", {"start": v(-15.2, -1.53) * mm, "end": v(-15.1, -1.43) * mm});
            skLineSegment(sketch, "E343", {"start": v(-15.1, -1.43) * mm, "end": v(-15.1, -1.4) * mm});
            skLineSegment(sketch, "E344", {"start": v(-15.1, -1.4) * mm, "end": v(-15.1, 0.32) * mm});
            skLineSegment(sketch, "E345", {"start": v(-15.1, 0.32) * mm, "end": v(-15.1, 0.33) * mm});
            skLineSegment(sketch, "E346", {"start": v(-15.1, 0.33) * mm, "end": v(-15.06, 0.38) * mm});
            skLineSegment(sketch, "E347", {"start": v(-15.06, 0.38) * mm, "end": v(-15.04, 0.38) * mm});
            skLineSegment(sketch, "E348", {"start": v(-15.04, 0.38) * mm, "end": v(-14.54, 0.38) * mm});
            skLineSegment(sketch, "E349", {"start": v(-14.54, 0.38) * mm, "end": v(-14.52, 0.38) * mm});
            skLineSegment(sketch, "E350", {"start": v(-14.52, 0.38) * mm, "end": v(-14.47, 0.33) * mm});
            skLineSegment(sketch, "E351", {"start": v(-14.47, 0.33) * mm, "end": v(-14.47, 0.32) * mm});
            skLineSegment(sketch, "E352", {"start": v(-14.47, 0.32) * mm, "end": v(-14.47, -1.4) * mm});
            skLineSegment(sketch, "E353", {"start": v(-14.47, -1.4) * mm, "end": v(-14.47, -1.43) * mm});
            skLineSegment(sketch, "E354", {"start": v(-14.47, -1.43) * mm, "end": v(-14.38, -1.53) * mm});
            skLineSegment(sketch, "E355", {"start": v(-14.38, -1.53) * mm, "end": v(-14.35, -1.53) * mm});
            skLineSegment(sketch, "E356", {"start": v(-14.35, -1.53) * mm, "end": v(-13.96, -1.53) * mm});
            skLineSegment(sketch, "E357", {"start": v(-13.96, -1.53) * mm, "end": v(-13.93, -1.53) * mm});
            skLineSegment(sketch, "E358", {"start": v(-13.93, -1.53) * mm, "end": v(-13.84, -1.43) * mm});
            skLineSegment(sketch, "E359", {"start": v(-13.84, -1.43) * mm, "end": v(-13.84, -1.4) * mm});
            skLineSegment(sketch, "E360", {"start": v(-13.84, -1.4) * mm, "end": v(-13.84, 0.32) * mm});
            skLineSegment(sketch, "E361", {"start": v(-13.84, 0.32) * mm, "end": v(-13.84, 0.32) * mm});
            skLineSegment(sketch, "E362", {"start": v(-13.84, 0.32) * mm, "end": v(-13.8, 0.38) * mm});
            skLineSegment(sketch, "E363", {"start": v(-13.8, 0.38) * mm, "end": v(-13.77, 0.38) * mm});
            skLineSegment(sketch, "E364", {"start": v(-13.77, 0.38) * mm, "end": v(-13.27, 0.38) * mm});
            skLineSegment(sketch, "E365", {"start": v(-13.27, 0.38) * mm, "end": v(-13.25, 0.38) * mm});
            skLineSegment(sketch, "E366", {"start": v(-13.25, 0.38) * mm, "end": v(-13.2, 0.33) * mm});
            skLineSegment(sketch, "E367", {"start": v(-13.2, 0.33) * mm, "end": v(-13.2, 0.32) * mm});
            skLineSegment(sketch, "E368", {"start": v(-13.2, 0.32) * mm, "end": v(-13.2, -1.4) * mm});
            skLineSegment(sketch, "E369", {"start": v(-13.2, -1.4) * mm, "end": v(-13.2, -1.43) * mm});
            skLineSegment(sketch, "E370", {"start": v(-13.2, -1.43) * mm, "end": v(-13.1, -1.53) * mm});
            skLineSegment(sketch, "E371", {"start": v(-13.1, -1.53) * mm, "end": v(-13.08, -1.53) * mm});
            skLineSegment(sketch, "E372", {"start": v(-13.08, -1.53) * mm, "end": v(-12.7, -1.53) * mm});
            skLineSegment(sketch, "E373", {"start": v(-12.7, -1.53) * mm, "end": v(-12.66, -1.53) * mm});
            skLineSegment(sketch, "E374", {"start": v(-12.66, -1.53) * mm, "end": v(-12.57, -1.43) * mm});
            skLineSegment(sketch, "E375", {"start": v(-12.57, -1.43) * mm, "end": v(-12.57, -1.4) * mm});
            skLineSegment(sketch, "E376", {"start": v(-12.57, -1.4) * mm, "end": v(-12.57, 0.89) * mm});
            skLineSegment(sketch, "E377", {"start": v(-12.57, 0.89) * mm, "end": v(-12.57, 0.92) * mm});
            skLineSegment(sketch, "E378", {"start": v(-12.57, 0.92) * mm, "end": v(-12.66, 1.01) * mm});
            skLineSegment(sketch, "E379", {"start": v(-12.66, 1.01) * mm, "end": v(-12.7, 1.01) * mm});
            skLineSegment(sketch, "E380", {"start": v(-11.17, -1.4) * mm, "end": v(-11.17, -1.43) * mm});
            skLineSegment(sketch, "E381", {"start": v(-11.17, -1.43) * mm, "end": v(-11.27, -1.53) * mm});
            skLineSegment(sketch, "E382", {"start": v(-11.27, -1.53) * mm, "end": v(-11.3, -1.53) * mm});
            skLineSegment(sketch, "E383", {"start": v(-11.3, -1.53) * mm, "end": v(-11.68, -1.53) * mm});
            skLineSegment(sketch, "E384", {"start": v(-11.68, -1.53) * mm, "end": v(-11.7, -1.53) * mm});
            skLineSegment(sketch, "E385", {"start": v(-11.7, -1.53) * mm, "end": v(-11.8, -1.43) * mm});
            skLineSegment(sketch, "E386", {"start": v(-11.8, -1.43) * mm, "end": v(-11.8, -1.4) * mm});
            skLineSegment(sketch, "E387", {"start": v(-11.8, -1.4) * mm, "end": v(-11.8, 0.89) * mm});
            skLineSegment(sketch, "E388", {"start": v(-11.8, 0.89) * mm, "end": v(-11.8, 0.92) * mm});
            skLineSegment(sketch, "E389", {"start": v(-11.8, 0.92) * mm, "end": v(-11.7, 1.01) * mm});
            skLineSegment(sketch, "E390", {"start": v(-11.7, 1.01) * mm, "end": v(-11.68, 1.01) * mm});
            skLineSegment(sketch, "E391", {"start": v(-11.68, 1.01) * mm, "end": v(-11.3, 1.01) * mm});
            skLineSegment(sketch, "E392", {"start": v(-11.3, 1.01) * mm, "end": v(-11.27, 1.01) * mm});
            skLineSegment(sketch, "E393", {"start": v(-11.27, 1.01) * mm, "end": v(-11.17, 0.92) * mm});
            skLineSegment(sketch, "E394", {"start": v(-11.17, 0.92) * mm, "end": v(-11.17, 0.89) * mm});
            skLineSegment(sketch, "E395", {"start": v(-11.17, 0.89) * mm, "end": v(-11.17, -1.4) * mm});
            skLineSegment(sketch, "E396", {"start": v(3.52, 0.13) * mm, "end": v(4.02, 0.13) * mm});
            skLineSegment(sketch, "E397", {"start": v(4.02, 0.13) * mm, "end": v(4.05, 0.13) * mm});
            skLineSegment(sketch, "E398", {"start": v(4.05, 0.13) * mm, "end": v(4.15, 0.03) * mm});
            skLineSegment(sketch, "E399", {"start": v(4.15, 0.03) * mm, "end": v(4.15, 0) * mm});
            skLineSegment(sketch, "E400", {"start": v(4.15, 0) * mm, "end": v(4.15, -0.5) * mm});
            skLineSegment(sketch, "E401", {"start": v(4.15, -0.5) * mm, "end": v(4.15, -0.54) * mm});
            skLineSegment(sketch, "E402", {"start": v(4.15, -0.54) * mm, "end": v(4.05, -0.63) * mm});
            skLineSegment(sketch, "E403", {"start": v(4.05, -0.63) * mm, "end": v(4.02, -0.63) * mm});
            skLineSegment(sketch, "E404", {"start": v(4.02, -0.63) * mm, "end": v(3.52, -0.63) * mm});
            skLineSegment(sketch, "E405", {"start": v(3.52, -0.63) * mm, "end": v(3.5, -0.63) * mm});
            skLineSegment(sketch, "E406", {"start": v(3.5, -0.63) * mm, "end": v(3.4, -0.54) * mm});
            skLineSegment(sketch, "E407", {"start": v(3.4, -0.54) * mm, "end": v(3.4, -0.5) * mm});
            skLineSegment(sketch, "E408", {"start": v(3.4, -0.5) * mm, "end": v(3.4, 0) * mm});
            skLineSegment(sketch, "E409", {"start": v(3.4, 0) * mm, "end": v(3.4, 0.03) * mm});
            skLineSegment(sketch, "E410", {"start": v(3.4, 0.03) * mm, "end": v(3.5, 0.13) * mm});
            skLineSegment(sketch, "E411", {"start": v(3.5, 0.13) * mm, "end": v(3.52, 0.13) * mm});
            skSolve(sketch);
        }
        {
            var Q0;
            Q0 = qSketchRegion(id + "F0", true);
            extrude(context, id + "F1", {"entities" : qUnion([Q0]), "depth" : 1.27 * mm});
        }
    });
